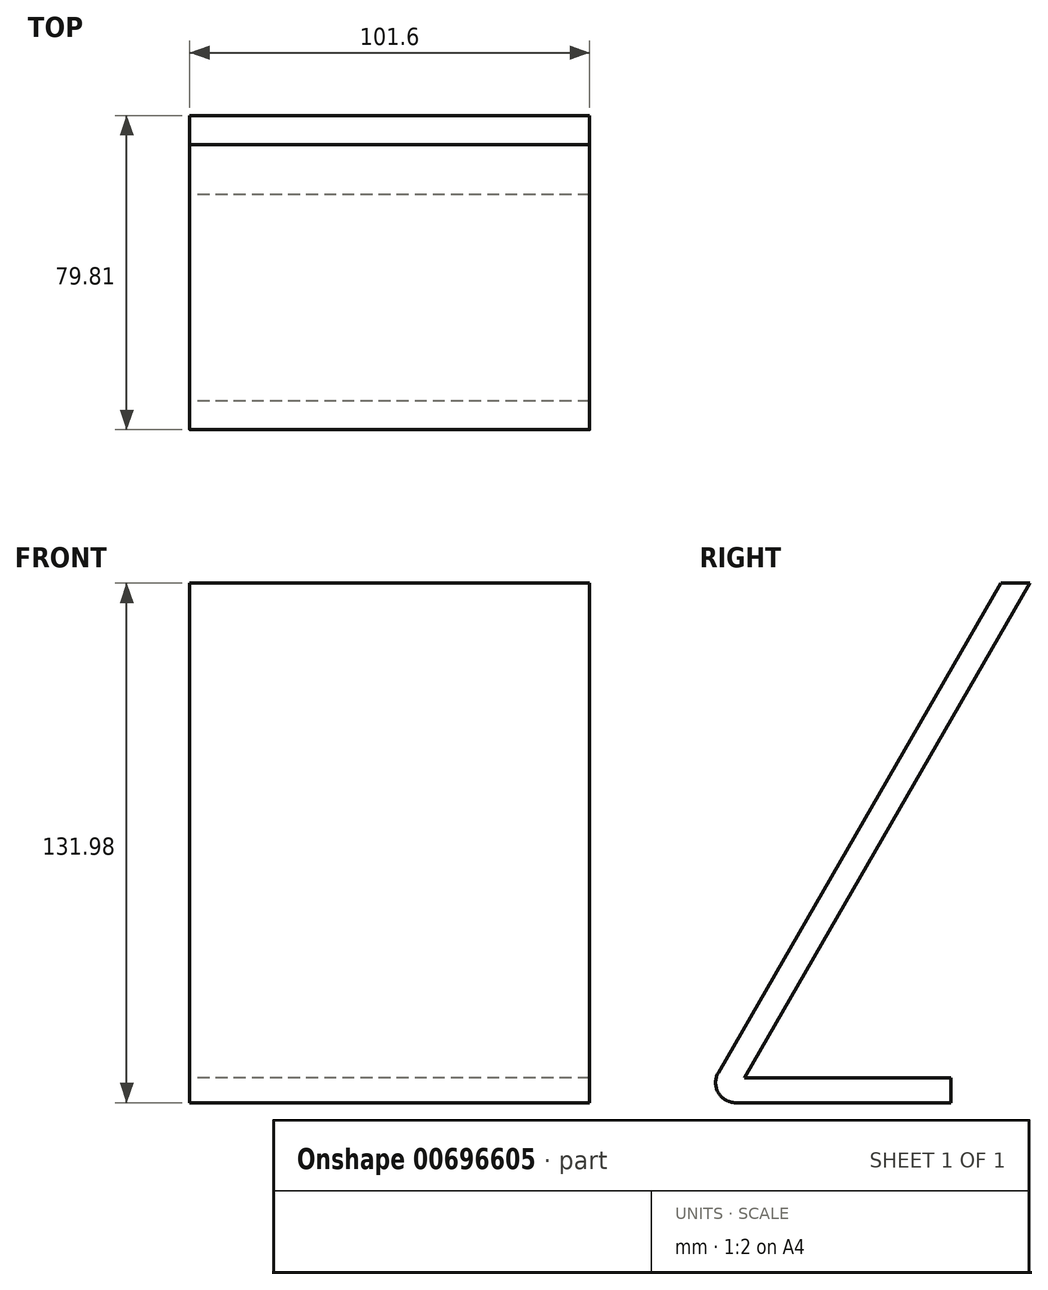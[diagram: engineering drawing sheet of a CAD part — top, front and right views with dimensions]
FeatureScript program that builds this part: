
annotation { "Feature Type Name" : "Feature", "Feature Type Description" : "" }
export const myFeature = defineFeature(function(context is Context, id is Id, definition is map)
    precondition{}
    {
        {
            var Q0;
            Q0=qCreatedBy(makeId("Right.planeOp"),FACE);
            var sketch = newSketch(context, id + "F0", { "sketchPlane" : qUnion([Q0])});
            skLineSegment(sketch, "E0", {"start": v(0, 0) * mm, "end": v(76.2, 131.98) * mm});
            skLineSegment(sketch, "E1", {"start": v(0, 0) * mm, "end": v(63.5, 0) * mm});
            skLineSegment(sketch, "E2.0", {"start": v(11, 6.35) * mm, "end": v(83.53, 131.98) * mm});
            skLineSegment(sketch, "E2.1", {"start": v(11, 6.35) * mm, "end": v(63.5, 6.35) * mm});
            skLineSegment(sketch, "E3", {"start": v(76.2, 131.98) * mm, "end": v(83.53, 131.98) * mm});
            skLineSegment(sketch, "E4", {"start": v(63.5, 6.35) * mm, "end": v(63.5, 0) * mm});
            skSolve(sketch);
        }
        {
            var Q0;
            Q0=makeQuery(id+"F0.imprint","IMPRINT",FACE,{"disambiguationData":[TD([[makeQuery(id+"F0.imprint","IMPRINT",EDGE,{"derivedFrom":sQuery(id+"F0.wireOp",EDGE,"E0")}),-1.0]])]});
            extrude(context, id + "F1", {"entities" : qUnion([Q0]), "endBound" : BoundingType.SYMMETRIC, "depth" : 101.6 * mm, "offsetDistance" : 25.4 * mm});
        }
        {
            var Q0;
            Q0=makeQuery(id+"F1.opExtrude","SWEPT_EDGE",EDGE,{"disambiguationData":[OSD([sQuery(id+"F0.wireOp",EDGE,"E0"),sQuery(id+"F0.wireOp",EDGE,"E1")])]});
            fillet(context, id + "F2", {"entities" : qUnion([Q0]), "radius" : 5.08 * mm, "tangentPropagation" : true, "allowEdgeOverflow" : false});
        }
    });
